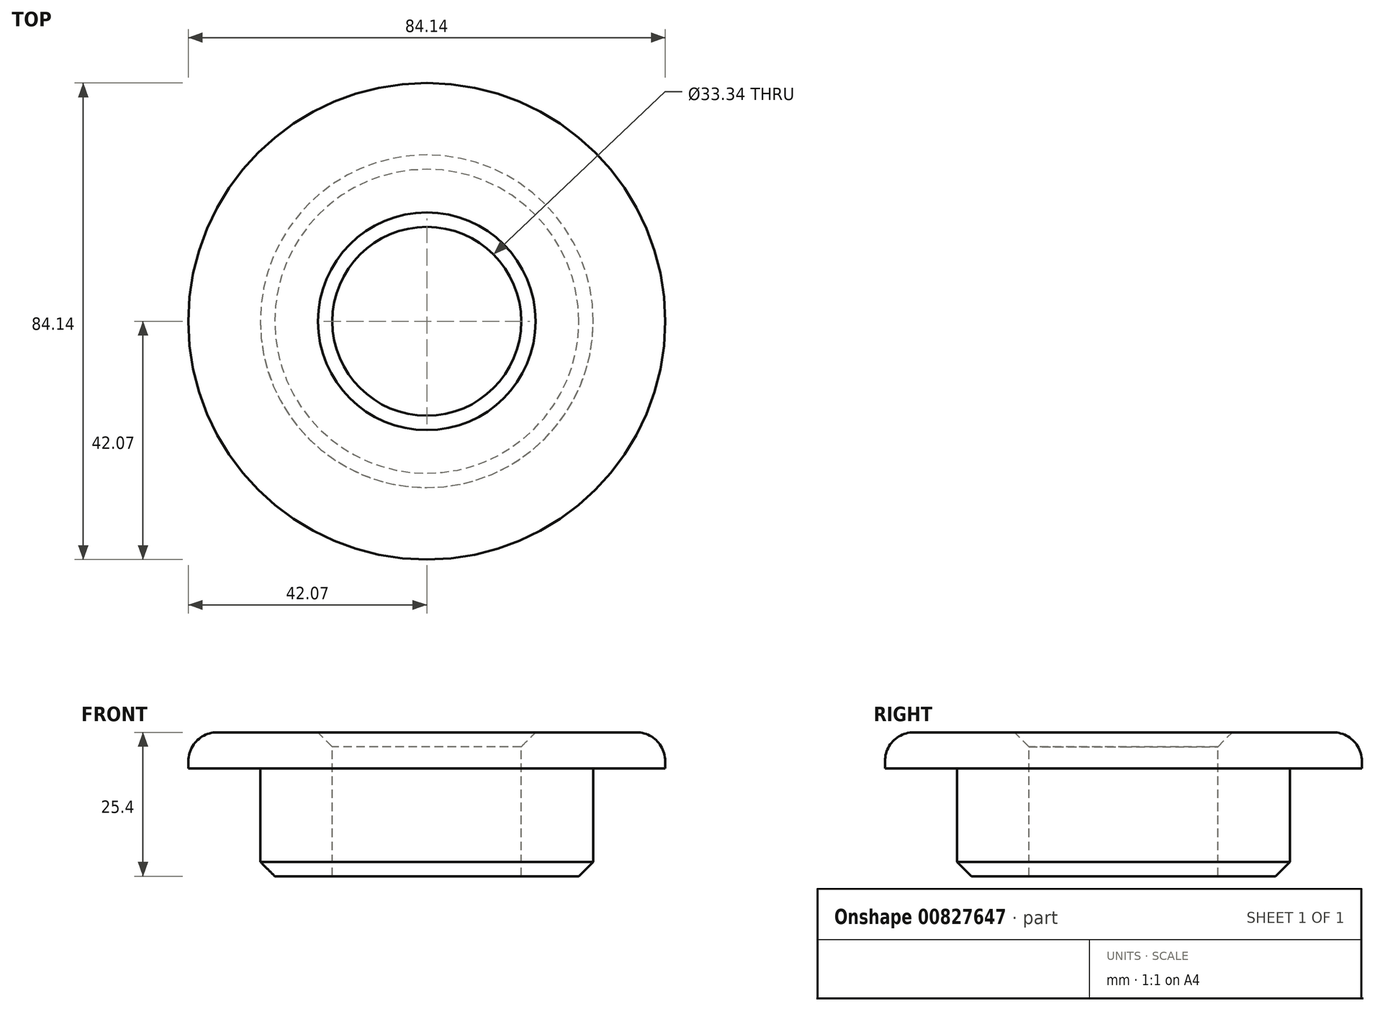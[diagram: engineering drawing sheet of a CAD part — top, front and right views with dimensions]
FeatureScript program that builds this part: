
annotation { "Feature Type Name" : "Feature", "Feature Type Description" : "" }
export const myFeature = defineFeature(function(context is Context, id is Id, definition is map)
    precondition{}
    {
        {
            var Q0;
            Q0=qCreatedBy(makeId("Front.planeOp"),FACE);
            var sketch = newSketch(context, id + "F0", { "sketchPlane" : qUnion([Q0])});
            skLineSegment(sketch, "E0.bottom", {"start": v(-29.37, 0) * mm, "end": v(-42.07, 0) * mm});
            skLineSegment(sketch, "E0.top", {"start": v(-16.67, 6.35) * mm, "end": v(-42.07, 6.35) * mm});
            skLineSegment(sketch, "E0.right", {"start": v(-42.07, 0) * mm, "end": v(-42.07, 6.35) * mm});
            skLineSegment(sketch, "E1.top", {"start": v(-29.37, -19.05) * mm, "end": v(-16.67, -19.05) * mm});
            skLineSegment(sketch, "E1.left", {"start": v(-29.37, 0) * mm, "end": v(-29.37, -19.05) * mm});
            skLineSegment(sketch, "E1.right", {"start": v(0, 0) * mm, "end": v(0, -19.05) * mm, "construction": true});
            skLineSegment(sketch, "E2", {"start": v(-16.67, 6.35) * mm, "end": v(-16.67, -19.05) * mm});
            skSolve(sketch);
        }
        {
            var Q0;
            Q0=makeQuery(id+"F0.imprint","IMPRINT",FACE,{"disambiguationData":[TD([[makeQuery(id+"F0.imprint","IMPRINT",EDGE,{"derivedFrom":sQuery(id+"F0.wireOp",EDGE,"E0.bottom")}),-1.0]])]});
            var Q1;
            Q1=sQuery(id+"F0.wireOp",EDGE,"E1.right");
            revolve(context, id + "F1", {"surfaceOperationType" : NewSurfaceOperationType.NEW, "entities" : qUnion([Q0]), "axis" : qUnion([Q1]), "revolveType" : RevolveType.FULL});
        }
        {
            var Q0;
            Q0=makeQuery(id+"F1.opRevolve","SWEPT_EDGE",EDGE,{"disambiguationData":[OSD([sQuery(id+"F0.wireOp",EDGE,"E0.top"),sQuery(id+"F0.wireOp",EDGE,"E0.right")])]});
            fillet(context, id + "F2", {"entities" : qUnion([Q0]), "radius" : 5.08 * mm, "tangentPropagation" : true, "allowEdgeOverflow" : false});
        }
        {
            var Q0;
            Q0=makeQuery(id+"F1.opRevolve","SWEPT_EDGE",EDGE,{"disambiguationData":[OSD([sQuery(id+"F0.wireOp",EDGE,"E0.top"),sQuery(id+"F0.wireOp",EDGE,"E2")])]});
            chamfer(context, id + "F3", {"entities" : qUnion([Q0]), "width" : 2.54 * mm, "tangentPropagation" : true});
        }
        {
            var Q0;
            Q0=makeQuery(id+"F1.opRevolve","SWEPT_EDGE",EDGE,{"disambiguationData":[OSD([sQuery(id+"F0.wireOp",EDGE,"E1.top"),sQuery(id+"F0.wireOp",EDGE,"E1.left")])]});
            chamfer(context, id + "F4", {"entities" : qUnion([Q0]), "width" : 2.54 * mm, "tangentPropagation" : true});
        }
    });
